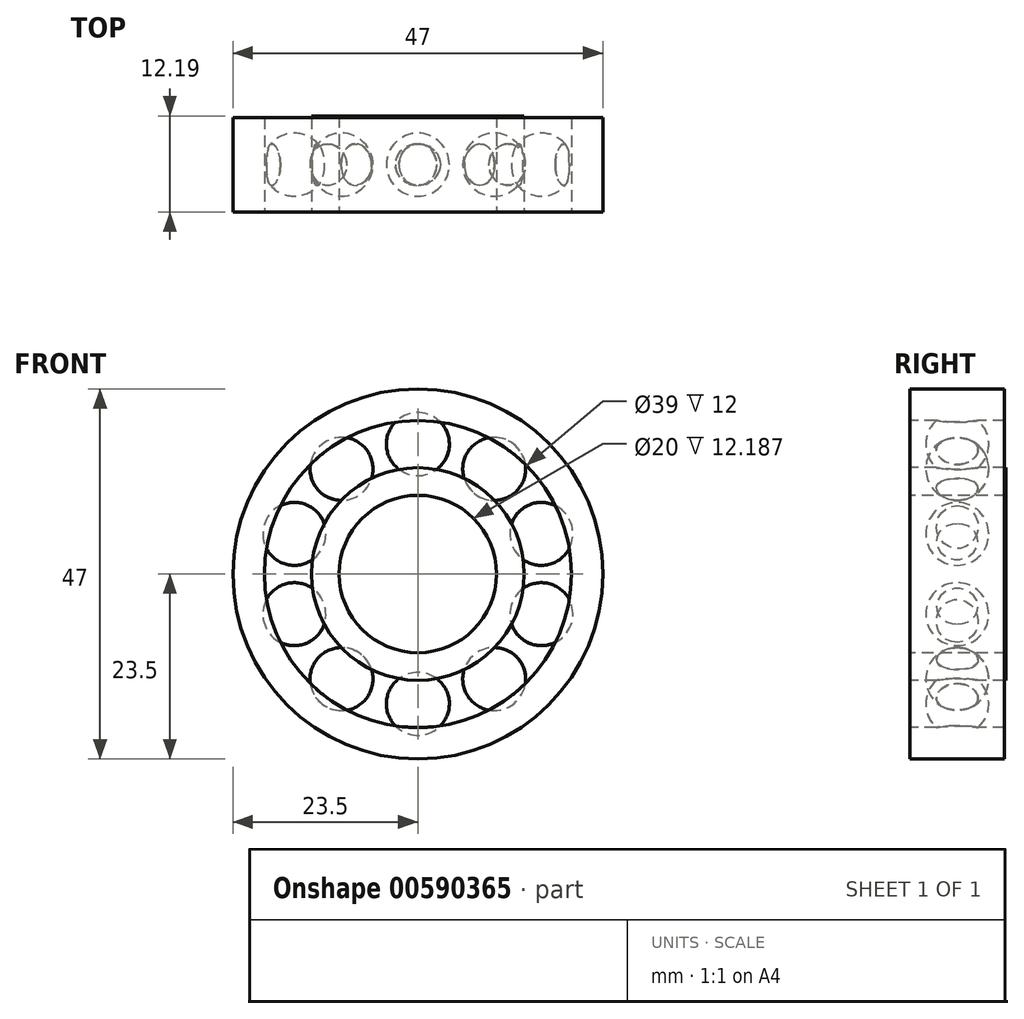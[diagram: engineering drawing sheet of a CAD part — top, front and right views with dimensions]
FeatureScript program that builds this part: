
annotation { "Feature Type Name" : "Feature", "Feature Type Description" : "" }
export const myFeature = defineFeature(function(context is Context, id is Id, definition is map)
    precondition{}
    {
        {
            var Q0;
            Q0=qCreatedBy(makeId("Right.planeOp"),FACE);
            var sketch = newSketch(context, id + "F0", { "sketchPlane" : qUnion([Q0])});
            skLineSegment(sketch, "E0.bottom", {"start": v(0, 23.5) * mm, "end": v(12, 23.5) * mm});
            skLineSegment(sketch, "E0.top", {"start": v(0, 19.5) * mm, "end": v(12, 19.5) * mm});
            skLineSegment(sketch, "E0.left", {"start": v(0, 23.5) * mm, "end": v(0, 19.5) * mm});
            skLineSegment(sketch, "E0.right", {"start": v(12, 23.5) * mm, "end": v(12, 19.5) * mm});
            skLineSegment(sketch, "E1.bottom", {"start": v(0, 13.5) * mm, "end": v(12.19, 13.5) * mm});
            skLineSegment(sketch, "E1.top", {"start": v(0, 10) * mm, "end": v(12.19, 10) * mm});
            skLineSegment(sketch, "E1.left", {"start": v(0, 13.5) * mm, "end": v(0, 10) * mm});
            skLineSegment(sketch, "E1.right", {"start": v(12.19, 13.5) * mm, "end": v(12.19, 10) * mm});
            skLineSegment(sketch, "E2", {"start": v(0, 0) * mm, "end": v(98.25, 0) * mm, "construction": true});
            skSolve(sketch);
        }
        {
            var Q0;
            Q0=makeQuery(id+"F0.imprint","IMPRINT",FACE,{"disambiguationData":[TD([[makeQuery(id+"F0.imprint","IMPRINT",EDGE,{"derivedFrom":sQuery(id+"F0.wireOp",EDGE,"E0.bottom")}),-1.0]])]});
            var Q1;
            Q1=makeQuery(id+"F0.imprint","IMPRINT",FACE,{"disambiguationData":[TD([[makeQuery(id+"F0.imprint","IMPRINT",EDGE,{"derivedFrom":sQuery(id+"F0.wireOp",EDGE,"E1.bottom")}),-1.0]])]});
            var Q2;
            Q2=sQuery(id+"F0.wireOp",EDGE,"E2");
            revolve(context, id + "F1", {"entities" : qUnion([Q0, Q1]), "axis" : qUnion([Q2]), "revolveType" : RevolveType.FULL});
        }
        {
            var Q0;
            Q0=qCreatedBy(makeId("Front.planeOp"),FACE);
            cPlane(context, id + "F2", {"entities" : qUnion([Q0]), "cplaneType" : CPlaneType.OFFSET, "offset" : 6 * mm, "oppositeDirection" : true, "width" : 150 * mm, "height" : 150 * mm});
        }
        {
            var Q0;
            Q0=qCreatedBy(id+"F2.planeOp",FACE);
            var sketch = newSketch(context, id + "F3", { "sketchPlane" : qUnion([Q0])});
            skArc(sketch, "E3", {"start": v(0, 12.5) * mm, "mid": v(4, 16.5) * mm, "end": v(0, 20.5) * mm});
            skLineSegment(sketch, "E4", {"start": v(0, 20.5) * mm, "end": v(0, 12.5) * mm});
            skPoint(sketch, "E5.orphan", {"position": v(0, 29.02) * mm});
            skSolve(sketch);
        }
        {
            var Q0;
            Q0 = qSketchRegion(id + "F3", true);
            var Q1;
            Q1=sQuery(id+"F3.wireOp",EDGE,"E4");
            revolve(context, id + "F4", {"entities" : qUnion([Q0]), "axis" : qUnion([Q1]), "revolveType" : RevolveType.FULL});
        }
        {
            var Q0;
            Q0=makeQuery(id+"F4.opRevolve","SWEPT_BODY",BODY,{"disambiguationData":[OSD([sQuery(id+"F3.wireOp",EDGE,"E3"),sQuery(id+"F3.wireOp",EDGE,"E4")])]});
            var Q1;
            Q1=makeQuery(id+"F1.opRevolve","SWEPT_EDGE",EDGE,{"disambiguationData":[OSD([sQuery(id+"F0.wireOp",EDGE,"E0.bottom"),sQuery(id+"F0.wireOp",EDGE,"E0.left")])]});
            circularPattern(context, id + "F5", {"operationType" : NewBodyOperationType.ADD, "entities" : qUnion([Q0]), "axis" : qUnion([Q1]), "angle" : 360 * degree, "instanceCount" : 10, "equalSpace" : true});
        }
    });
